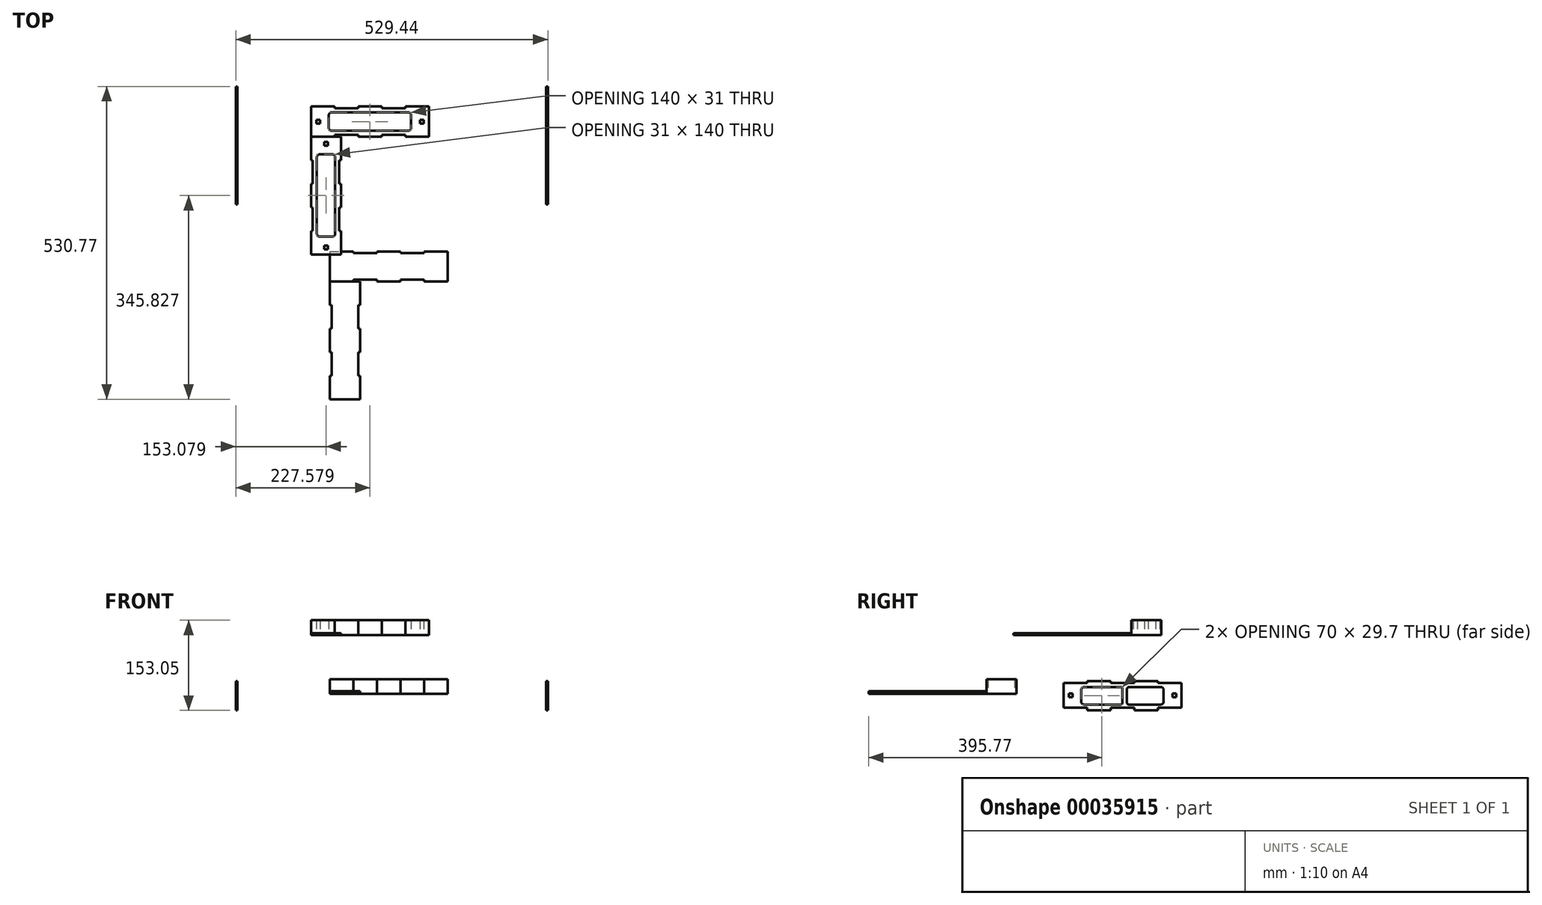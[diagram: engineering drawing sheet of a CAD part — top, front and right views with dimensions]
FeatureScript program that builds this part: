
annotation { "Feature Type Name" : "Feature", "Feature Type Description" : "" }
export const myFeature = defineFeature(function(context is Context, id is Id, definition is map)
    precondition{}
    {
        {
            var Q0;
            Q0=qCreatedBy(makeId("Top.planeOp"),FACE);
            cPlane(context, id + "F0", {"entities" : qUnion([Q0]), "cplaneType" : CPlaneType.OFFSET, "offset" : 100 * mm, "width" : 150 * mm, "height" : 150 * mm});
        }
        {
            var Q0;
            Q0=qCreatedBy(id+"F0.planeOp",FACE);
            var sketch = newSketch(context, id + "F1", { "sketchPlane" : qUnion([Q0])});
            skLineSegment(sketch, "E0", {"start": v(-137.14, 13.06) * mm, "end": v(-97.14, 13.06) * mm});
            skLineSegment(sketch, "E1", {"start": v(-97.14, 13.06) * mm, "end": v(-97.14, 10.06) * mm});
            skLineSegment(sketch, "E2", {"start": v(-97.14, 10.06) * mm, "end": v(-57.14, 10.06) * mm});
            skLineSegment(sketch, "E3", {"start": v(-57.14, 10.06) * mm, "end": v(-57.14, 13.06) * mm});
            skLineSegment(sketch, "E4", {"start": v(-57.14, 13.06) * mm, "end": v(-17.14, 13.06) * mm});
            skLineSegment(sketch, "E5", {"start": v(-17.14, 13.06) * mm, "end": v(-17.14, 10.06) * mm});
            skLineSegment(sketch, "E6", {"start": v(-17.14, 10.06) * mm, "end": v(22.86, 10.06) * mm});
            skLineSegment(sketch, "E7", {"start": v(22.86, 10.06) * mm, "end": v(22.86, 13.06) * mm});
            skLineSegment(sketch, "E8", {"start": v(22.86, 13.06) * mm, "end": v(62.86, 13.06) * mm});
            skLineSegment(sketch, "E9", {"start": v(62.86, 13.06) * mm, "end": v(62.86, -37.94) * mm});
            skLineSegment(sketch, "E10", {"start": v(62.86, -37.94) * mm, "end": v(22.86, -37.94) * mm});
            skLineSegment(sketch, "E11", {"start": v(22.86, -37.94) * mm, "end": v(22.86, -34.94) * mm});
            skLineSegment(sketch, "E12", {"start": v(22.86, -34.94) * mm, "end": v(-17.14, -34.94) * mm});
            skLineSegment(sketch, "E13", {"start": v(-17.14, -34.94) * mm, "end": v(-17.14, -37.94) * mm});
            skLineSegment(sketch, "E14", {"start": v(-17.14, -37.94) * mm, "end": v(-57.14, -37.94) * mm});
            skLineSegment(sketch, "E15", {"start": v(-57.14, -37.94) * mm, "end": v(-57.14, -34.94) * mm});
            skLineSegment(sketch, "E16", {"start": v(-57.14, -34.94) * mm, "end": v(-97.14, -34.94) * mm});
            skLineSegment(sketch, "E17", {"start": v(-97.14, -34.94) * mm, "end": v(-97.14, -37.94) * mm});
            skLineSegment(sketch, "E18", {"start": v(-97.14, -37.94) * mm, "end": v(-137.14, -37.94) * mm});
            skLineSegment(sketch, "E19", {"start": v(-137.14, 13.06) * mm, "end": v(-137.14, -37.94) * mm});
            skLineSegment(sketch, "E20.bottom", {"start": v(-102.14, -27.94) * mm, "end": v(27.86, -27.94) * mm});
            skLineSegment(sketch, "E20.top", {"start": v(-102.14, 3.06) * mm, "end": v(27.86, 3.06) * mm});
            skLineSegment(sketch, "E20.left", {"start": v(-107.14, -22.94) * mm, "end": v(-107.14, -1.94) * mm});
            skLineSegment(sketch, "E20.right", {"start": v(32.86, -22.94) * mm, "end": v(32.86, -1.94) * mm});
            skPoint(sketch, "E21.visualSharp", {"position": v(-107.14, 3.06) * mm});
            skArc(sketch, "E21.filletArc", {"start": v(-102.14, 3.06) * mm, "mid": v(-105.68, 1.6) * mm, "end": v(-107.14, -1.94) * mm});
            skPoint(sketch, "E22.visualSharp", {"position": v(-107.14, -27.94) * mm});
            skArc(sketch, "E22.filletArc", {"start": v(-107.14, -22.94) * mm, "mid": v(-105.68, -26.48) * mm, "end": v(-102.14, -27.94) * mm});
            skPoint(sketch, "E23.visualSharp", {"position": v(32.86, 3.06) * mm});
            skArc(sketch, "E23.filletArc", {"start": v(32.86, -1.94) * mm, "mid": v(31.4, 1.6) * mm, "end": v(27.86, 3.06) * mm});
            skPoint(sketch, "E24.visualSharp", {"position": v(32.86, -27.94) * mm});
            skArc(sketch, "E24.filletArc", {"start": v(27.86, -27.94) * mm, "mid": v(31.4, -26.48) * mm, "end": v(32.86, -22.94) * mm});
            skLineSegment(sketch, "E25.rect.bottom", {"start": v(47.7, -15.6) * mm, "end": v(54, -15.6) * mm});
            skLineSegment(sketch, "E25.rect.top", {"start": v(47.7, -9.3) * mm, "end": v(54, -9.3) * mm});
            skLineSegment(sketch, "E25.rect.left", {"start": v(47.7, -15.6) * mm, "end": v(47.7, -9.3) * mm});
            skLineSegment(sketch, "E25.rect.right", {"start": v(54, -15.6) * mm, "end": v(54, -9.3) * mm});
            skPoint(sketch, "E25.rect.middle", {"position": v(50.86, -12.44) * mm});
            skPoint(sketch, "E25.rect.middle.positionSnap0", {"position": v(62.86, -12.44) * mm});
            skPoint(sketch, "E25.rect.centerSnap0", {"position": v(62.86, -12.44) * mm});
            skLineSegment(sketch, "E26.rect.bottom", {"start": v(-128.3, -15.6) * mm, "end": v(-122, -15.6) * mm});
            skLineSegment(sketch, "E26.rect.top", {"start": v(-128.3, -9.3) * mm, "end": v(-122, -9.3) * mm});
            skLineSegment(sketch, "E26.rect.left", {"start": v(-128.3, -15.6) * mm, "end": v(-128.3, -9.3) * mm});
            skLineSegment(sketch, "E26.rect.right", {"start": v(-122, -15.6) * mm, "end": v(-122, -9.3) * mm});
            skPoint(sketch, "E26.rect.middle", {"position": v(-125.14, -12.44) * mm});
            skPoint(sketch, "E26.rect.middle.positionSnap0", {"position": v(-137.14, -12.44) * mm});
            skPoint(sketch, "E26.rect.centerSnap0", {"position": v(-137.14, -12.44) * mm});
            skSolve(sketch);
        }
        {
            var Q0;
            Q0 = qSketchRegion(id + "F1", true);
            extrude(context, id + "F2", {"entities" : qUnion([Q0]), "depth" : 3 * mm});
        }
        {
            var Q0;
            Q0=qCreatedBy(makeId("Front.planeOp"),FACE);
            cPlane(context, id + "F3", {"entities" : qUnion([Q0]), "cplaneType" : CPlaneType.OFFSET, "offset" : 150 * mm, "width" : 150 * mm, "height" : 150 * mm});
        }
        {
            var Q0;
            Q0=qCreatedBy(id+"F3.planeOp",FACE);
            var sketch = newSketch(context, id + "F4", { "sketchPlane" : qUnion([Q0])});
            skLineSegment(sketch, "E27", {"start": v(-261.72, -23.35) * mm, "end": v(-261.72, 18.65) * mm});
            skLineSegment(sketch, "E28", {"start": v(-261.72, 18.65) * mm, "end": v(-221.72, 18.65) * mm});
            skLineSegment(sketch, "E29", {"start": v(-221.72, 18.65) * mm, "end": v(-221.72, 21.65) * mm});
            skLineSegment(sketch, "E30", {"start": v(-221.72, 21.65) * mm, "end": v(-181.72, 21.65) * mm});
            skLineSegment(sketch, "E31", {"start": v(-181.72, 21.65) * mm, "end": v(-181.72, 18.65) * mm});
            skLineSegment(sketch, "E32", {"start": v(-181.72, 18.65) * mm, "end": v(-141.72, 18.65) * mm});
            skLineSegment(sketch, "E33", {"start": v(-141.72, 18.65) * mm, "end": v(-141.72, 21.65) * mm});
            skLineSegment(sketch, "E34", {"start": v(-141.72, 21.65) * mm, "end": v(-101.72, 21.65) * mm});
            skLineSegment(sketch, "E35", {"start": v(-101.72, 21.65) * mm, "end": v(-101.72, 18.65) * mm});
            skLineSegment(sketch, "E36", {"start": v(-101.72, 18.65) * mm, "end": v(-61.72, 18.65) * mm});
            skLineSegment(sketch, "E37", {"start": v(-61.72, 18.65) * mm, "end": v(-61.72, -23.35) * mm});
            skLineSegment(sketch, "E38", {"start": v(-61.72, -23.35) * mm, "end": v(-101.72, -23.35) * mm});
            skLineSegment(sketch, "E39", {"start": v(-101.72, -23.35) * mm, "end": v(-101.72, -28.05) * mm});
            skLineSegment(sketch, "E40", {"start": v(-101.72, -28.05) * mm, "end": v(-141.72, -28.05) * mm});
            skLineSegment(sketch, "E41", {"start": v(-141.72, -28.05) * mm, "end": v(-141.72, -23.35) * mm});
            skLineSegment(sketch, "E42", {"start": v(-141.72, -23.35) * mm, "end": v(-181.72, -23.35) * mm});
            skLineSegment(sketch, "E43", {"start": v(-181.72, -23.35) * mm, "end": v(-181.72, -28.05) * mm});
            skLineSegment(sketch, "E44", {"start": v(-181.72, -28.05) * mm, "end": v(-221.72, -28.05) * mm});
            skLineSegment(sketch, "E45", {"start": v(-221.72, -28.05) * mm, "end": v(-221.72, -23.35) * mm});
            skLineSegment(sketch, "E46", {"start": v(-221.72, -23.35) * mm, "end": v(-261.72, -23.35) * mm});
            skLineSegment(sketch, "E47.bottom", {"start": v(-226.72, 11.65) * mm, "end": v(-164.72, 11.65) * mm});
            skLineSegment(sketch, "E47.top", {"start": v(-226.72, -18.05) * mm, "end": v(-164.72, -18.05) * mm});
            skLineSegment(sketch, "E47.left", {"start": v(-231.72, 6.65) * mm, "end": v(-231.72, -13.05) * mm});
            skLineSegment(sketch, "E47.right", {"start": v(-161.72, 8.65) * mm, "end": v(-161.72, -15.05) * mm});
            skLineSegment(sketch, "E48.bottom", {"start": v(-150.95, 11.65) * mm, "end": v(-96.72, 11.65) * mm});
            skLineSegment(sketch, "E48.top", {"start": v(-150.95, -18.05) * mm, "end": v(-96.72, -18.05) * mm});
            skLineSegment(sketch, "E48.left", {"start": v(-153.95, 8.65) * mm, "end": v(-153.95, -15.05) * mm});
            skLineSegment(sketch, "E48.right", {"start": v(-91.72, 6.65) * mm, "end": v(-91.72, -13.05) * mm});
            skPoint(sketch, "E49.visualSharp", {"position": v(-231.72, 11.65) * mm});
            skArc(sketch, "E49.filletArc", {"start": v(-226.72, 11.65) * mm, "mid": v(-230.26, 10.18) * mm, "end": v(-231.72, 6.65) * mm});
            skPoint(sketch, "E50.visualSharp", {"position": v(-231.72, -18.05) * mm});
            skArc(sketch, "E50.filletArc", {"start": v(-231.72, -13.05) * mm, "mid": v(-230.26, -16.59) * mm, "end": v(-226.72, -18.05) * mm});
            skPoint(sketch, "E51.visualSharp", {"position": v(-91.72, 11.65) * mm});
            skArc(sketch, "E51.filletArc", {"start": v(-91.72, 6.65) * mm, "mid": v(-93.18, 10.18) * mm, "end": v(-96.72, 11.65) * mm});
            skPoint(sketch, "E52.visualSharp", {"position": v(-91.72, -18.05) * mm});
            skArc(sketch, "E52.filletArc", {"start": v(-96.72, -18.05) * mm, "mid": v(-93.18, -16.59) * mm, "end": v(-91.72, -13.05) * mm});
            skPoint(sketch, "E53.visualSharp", {"position": v(-153.95, 11.65) * mm});
            skArc(sketch, "E53.filletArc", {"start": v(-150.95, 11.65) * mm, "mid": v(-153.07, 10.77) * mm, "end": v(-153.95, 8.65) * mm});
            skPoint(sketch, "E54.visualSharp", {"position": v(-153.95, -18.05) * mm});
            skArc(sketch, "E54.filletArc", {"start": v(-153.95, -15.05) * mm, "mid": v(-153.07, -17.18) * mm, "end": v(-150.95, -18.05) * mm});
            skPoint(sketch, "E55.visualSharp", {"position": v(-161.72, -18.05) * mm});
            skArc(sketch, "E55.filletArc", {"start": v(-164.72, -18.05) * mm, "mid": v(-162.6, -17.18) * mm, "end": v(-161.72, -15.05) * mm});
            skPoint(sketch, "E56.visualSharp", {"position": v(-161.72, 11.65) * mm});
            skArc(sketch, "E56.filletArc", {"start": v(-161.72, 8.65) * mm, "mid": v(-162.6, 10.77) * mm, "end": v(-164.72, 11.65) * mm});
            skLineSegment(sketch, "E57.rect.bottom", {"start": v(-246.57, 0.8) * mm, "end": v(-252.87, 0.8) * mm});
            skLineSegment(sketch, "E57.rect.top", {"start": v(-246.57, -5.5) * mm, "end": v(-252.87, -5.5) * mm});
            skLineSegment(sketch, "E57.rect.left", {"start": v(-246.57, 0.8) * mm, "end": v(-246.57, -5.5) * mm});
            skLineSegment(sketch, "E57.rect.right", {"start": v(-252.87, 0.8) * mm, "end": v(-252.87, -5.5) * mm});
            skPoint(sketch, "E57.rect.middle", {"position": v(-249.72, -2.35) * mm});
            skPoint(sketch, "E57.rect.middle.positionSnap0", {"position": v(-261.72, -2.35) * mm});
            skPoint(sketch, "E57.rect.centerSnap0", {"position": v(-261.72, -2.35) * mm});
            skLineSegment(sketch, "E58.rect.bottom", {"start": v(-70.57, 0.8) * mm, "end": v(-76.87, 0.8) * mm});
            skLineSegment(sketch, "E58.rect.top", {"start": v(-70.57, -5.5) * mm, "end": v(-76.87, -5.5) * mm});
            skLineSegment(sketch, "E58.rect.left", {"start": v(-70.57, 0.8) * mm, "end": v(-70.57, -5.5) * mm});
            skLineSegment(sketch, "E58.rect.right", {"start": v(-76.87, 0.8) * mm, "end": v(-76.87, -5.5) * mm});
            skPoint(sketch, "E58.rect.middle", {"position": v(-73.72, -2.35) * mm});
            skPoint(sketch, "E58.rect.middle.positionSnap0", {"position": v(-61.72, -2.35) * mm});
            skPoint(sketch, "E58.rect.centerSnap0", {"position": v(-61.72, -2.35) * mm});
            skSolve(sketch);
        }
        {
            var Q0;
            Q0 = qSketchRegion(id + "F4", true);
            extrude(context, id + "F5", {"entities" : qUnion([Q0]), "depth" : 3 * mm});
        }
        {
            var Q0;
            Q0=qCreatedBy(makeId("Top.planeOp"),FACE);
            var sketch = newSketch(context, id + "F6", { "sketchPlane" : qUnion([Q0])});
            skLineSegment(sketch, "E59", {"start": v(94.97, -232.77) * mm, "end": v(94.97, -283.77) * mm});
            skLineSegment(sketch, "E60", {"start": v(54.97, -232.77) * mm, "end": v(94.97, -232.77) * mm});
            skLineSegment(sketch, "E61", {"start": v(14.97, -283.77) * mm, "end": v(-25.03, -283.77) * mm});
            skLineSegment(sketch, "E62", {"start": v(14.97, -235.77) * mm, "end": v(54.97, -235.77) * mm});
            skLineSegment(sketch, "E63", {"start": v(-105.03, -232.77) * mm, "end": v(-105.03, -283.77) * mm});
            skLineSegment(sketch, "E64", {"start": v(-65.03, -283.77) * mm, "end": v(-105.03, -283.77) * mm});
            skLineSegment(sketch, "E65", {"start": v(-25.03, -280.77) * mm, "end": v(-65.03, -280.77) * mm});
            skLineSegment(sketch, "E66", {"start": v(54.97, -280.77) * mm, "end": v(14.97, -280.77) * mm});
            skLineSegment(sketch, "E67", {"start": v(94.97, -283.77) * mm, "end": v(54.97, -283.77) * mm});
            skLineSegment(sketch, "E68", {"start": v(-105.03, -232.77) * mm, "end": v(-65.03, -232.77) * mm});
            skLineSegment(sketch, "E69", {"start": v(-65.03, -235.77) * mm, "end": v(-25.03, -235.77) * mm});
            skLineSegment(sketch, "E70", {"start": v(-25.03, -232.77) * mm, "end": v(14.97, -232.77) * mm});
            skLineSegment(sketch, "E71", {"start": v(14.97, -232.77) * mm, "end": v(14.97, -235.77) * mm});
            skLineSegment(sketch, "E72", {"start": v(-65.03, -280.77) * mm, "end": v(-65.03, -283.77) * mm});
            skLineSegment(sketch, "E73", {"start": v(54.97, -235.77) * mm, "end": v(54.97, -232.77) * mm});
            skLineSegment(sketch, "E74", {"start": v(14.97, -280.77) * mm, "end": v(14.97, -283.77) * mm});
            skLineSegment(sketch, "E75", {"start": v(54.97, -283.77) * mm, "end": v(54.97, -280.77) * mm});
            skLineSegment(sketch, "E76", {"start": v(-25.03, -283.77) * mm, "end": v(-25.03, -280.77) * mm});
            skLineSegment(sketch, "E77", {"start": v(-65.03, -232.77) * mm, "end": v(-65.03, -235.77) * mm});
            skLineSegment(sketch, "E78", {"start": v(-25.03, -235.77) * mm, "end": v(-25.03, -232.77) * mm});
            skSolve(sketch);
        }
        {
            var Q0;
            Q0=makeQuery(id+"F6.imprint","IMPRINT",FACE,{"disambiguationData":[TD([[makeQuery(id+"F6.imprint","IMPRINT",EDGE,{"derivedFrom":sQuery(id+"F6.wireOp",EDGE,"E59")}),-1.0]])]});
            extrude(context, id + "F7", {"entities" : qUnion([Q0]), "depth" : 4.7 * mm});
        }
        {
            var Q0;
            Q0=makeQuery(id+"F2.opExtrude","SWEPT_BODY",BODY,{"disambiguationData":[OSD([sQuery(id+"F1.wireOp",EDGE,"E0"),sQuery(id+"F1.wireOp",EDGE,"E1"),sQuery(id+"F1.wireOp",EDGE,"E2"),sQuery(id+"F1.wireOp",EDGE,"E3"),sQuery(id+"F1.wireOp",EDGE,"E4"),sQuery(id+"F1.wireOp",EDGE,"E5"),sQuery(id+"F1.wireOp",EDGE,"E6"),sQuery(id+"F1.wireOp",EDGE,"E7"),sQuery(id+"F1.wireOp",EDGE,"E8"),sQuery(id+"F1.wireOp",EDGE,"E9"),sQuery(id+"F1.wireOp",EDGE,"E10"),sQuery(id+"F1.wireOp",EDGE,"E11"),sQuery(id+"F1.wireOp",EDGE,"E12"),sQuery(id+"F1.wireOp",EDGE,"E13"),sQuery(id+"F1.wireOp",EDGE,"E14"),sQuery(id+"F1.wireOp",EDGE,"E15"),sQuery(id+"F1.wireOp",EDGE,"E16"),sQuery(id+"F1.wireOp",EDGE,"E17"),sQuery(id+"F1.wireOp",EDGE,"E18"),sQuery(id+"F1.wireOp",EDGE,"E19"),sQuery(id+"F1.wireOp",EDGE,"E20.bottom"),sQuery(id+"F1.wireOp",EDGE,"E20.top"),sQuery(id+"F1.wireOp",EDGE,"E20.left"),sQuery(id+"F1.wireOp",EDGE,"E20.right"),sQuery(id+"F1.wireOp",EDGE,"E21.filletArc"),sQuery(id+"F1.wireOp",EDGE,"E22.filletArc"),sQuery(id+"F1.wireOp",EDGE,"E23.filletArc"),sQuery(id+"F1.wireOp",EDGE,"E24.filletArc")])]});
            var Q1;
            Q1=makeQuery(id+"F2.opExtrude","SWEPT_EDGE",EDGE,{"disambiguationData":[OSD([sQuery(id+"F1.wireOp",EDGE,"E18"),sQuery(id+"F1.wireOp",EDGE,"E19")])]});
            transform(context, id + "F8", {"entities" : qUnion([Q0]), "transformType" : TransformType.ROTATION, "transformAxis" : qUnion([Q1]), "angle" : 90 * degree, "makeCopy" : false});
        }
        {
            var Q0;
            Q0=makeQuery(id+"F7.opExtrude","SWEPT_BODY",BODY,{"disambiguationData":[OSD([sQuery(id+"F6.wireOp",EDGE,"E59"),sQuery(id+"F6.wireOp",EDGE,"E60"),sQuery(id+"F6.wireOp",EDGE,"E61"),sQuery(id+"F6.wireOp",EDGE,"E62"),sQuery(id+"F6.wireOp",EDGE,"E63"),sQuery(id+"F6.wireOp",EDGE,"E64"),sQuery(id+"F6.wireOp",EDGE,"E65"),sQuery(id+"F6.wireOp",EDGE,"E66"),sQuery(id+"F6.wireOp",EDGE,"E67"),sQuery(id+"F6.wireOp",EDGE,"E68"),sQuery(id+"F6.wireOp",EDGE,"E69"),sQuery(id+"F6.wireOp",EDGE,"E70"),sQuery(id+"F6.wireOp",EDGE,"E71"),sQuery(id+"F6.wireOp",EDGE,"E72"),sQuery(id+"F6.wireOp",EDGE,"E73"),sQuery(id+"F6.wireOp",EDGE,"E74"),sQuery(id+"F6.wireOp",EDGE,"E75"),sQuery(id+"F6.wireOp",EDGE,"E76"),sQuery(id+"F6.wireOp",EDGE,"E77"),sQuery(id+"F6.wireOp",EDGE,"E78")])]});
            var Q1;
            Q1=makeQuery(id+"F7.opExtrude","SWEPT_EDGE",EDGE,{"disambiguationData":[OSD([sQuery(id+"F6.wireOp",EDGE,"E63"),sQuery(id+"F6.wireOp",EDGE,"E64")])]});
            transform(context, id + "F9", {"entities" : qUnion([Q0]), "transformType" : TransformType.ROTATION, "transformAxis" : qUnion([Q1]), "angle" : 90 * degree, "makeCopy" : false});
        }
        {
            var Q0;
            Q0=makeQuery(id+"F5.opExtrude","SWEPT_BODY",BODY,{"disambiguationData":[OSD([sQuery(id+"F4.wireOp",EDGE,"E27"),sQuery(id+"F4.wireOp",EDGE,"E28"),sQuery(id+"F4.wireOp",EDGE,"E29"),sQuery(id+"F4.wireOp",EDGE,"E30"),sQuery(id+"F4.wireOp",EDGE,"E31"),sQuery(id+"F4.wireOp",EDGE,"E32"),sQuery(id+"F4.wireOp",EDGE,"E33"),sQuery(id+"F4.wireOp",EDGE,"E34"),sQuery(id+"F4.wireOp",EDGE,"E35"),sQuery(id+"F4.wireOp",EDGE,"E36"),sQuery(id+"F4.wireOp",EDGE,"E37"),sQuery(id+"F4.wireOp",EDGE,"E38"),sQuery(id+"F4.wireOp",EDGE,"E39"),sQuery(id+"F4.wireOp",EDGE,"E40"),sQuery(id+"F4.wireOp",EDGE,"E41"),sQuery(id+"F4.wireOp",EDGE,"E42"),sQuery(id+"F4.wireOp",EDGE,"E43"),sQuery(id+"F4.wireOp",EDGE,"E44"),sQuery(id+"F4.wireOp",EDGE,"E45"),sQuery(id+"F4.wireOp",EDGE,"E46"),sQuery(id+"F4.wireOp",EDGE,"7fbabfab-6c45-4351-a13d-65926b73b169.bottom"),sQuery(id+"F4.wireOp",EDGE,"7fbabfab-6c45-4351-a13d-65926b73b169.top"),sQuery(id+"F4.wireOp",EDGE,"7fbabfab-6c45-4351-a13d-65926b73b169.left"),sQuery(id+"F4.wireOp",EDGE,"7fbabfab-6c45-4351-a13d-65926b73b169.right"),sQuery(id+"F4.wireOp",EDGE,"bc9e853f-3614-4c7b-95ac-c1f526d06f9d.bottom"),sQuery(id+"F4.wireOp",EDGE,"bc9e853f-3614-4c7b-95ac-c1f526d06f9d.top"),sQuery(id+"F4.wireOp",EDGE,"bc9e853f-3614-4c7b-95ac-c1f526d06f9d.left"),sQuery(id+"F4.wireOp",EDGE,"bc9e853f-3614-4c7b-95ac-c1f526d06f9d.right"),sQuery(id+"F4.wireOp",EDGE,"9d363461-d9c7-42ad-a605-f10a583b7adf.filletArc"),sQuery(id+"F4.wireOp",EDGE,"a8185aef-b156-4268-98df-fd60d99d2e8b.filletArc"),sQuery(id+"F4.wireOp",EDGE,"17aa48d8-23c2-4526-90ac-4948f552f9d6.filletArc"),sQuery(id+"F4.wireOp",EDGE,"ec2dc547-445c-4b10-b0b5-5fbef85a2b8e.filletArc"),sQuery(id+"F4.wireOp",EDGE,"308059fb-494a-4663-8d27-ab8e5de39cd5.filletArc"),sQuery(id+"F4.wireOp",EDGE,"7f48fe49-b43d-4b02-bc32-553ec1c7f7b5.filletArc"),sQuery(id+"F4.wireOp",EDGE,"39a5a2ae-93e5-4ad9-8a0c-e8c8752d564a.filletArc"),sQuery(id+"F4.wireOp",EDGE,"36d556c5-8a39-45bb-97b7-d6d2a9260684.filletArc")])]});
            var Q1;
            Q1=makeQuery(id+"F5.opExtrude","CAP_EDGE",EDGE,{"disambiguationData":[OSD([sQuery(id+"F4.wireOp",EDGE,"E27")])],"isStart":false});
            transform(context, id + "F10", {"entities" : qUnion([Q0]), "transformType" : TransformType.ROTATION, "transformAxis" : qUnion([Q1]), "angle" : 90 * degree, "makeCopy" : false});
        }
        {
            var Q0;
            Q0=makeQuery(id+"F5.opExtrude","SWEPT_BODY",BODY,{"disambiguationData":[OSD([sQuery(id+"F4.wireOp",EDGE,"E27"),sQuery(id+"F4.wireOp",EDGE,"E28"),sQuery(id+"F4.wireOp",EDGE,"E29"),sQuery(id+"F4.wireOp",EDGE,"E30"),sQuery(id+"F4.wireOp",EDGE,"E31"),sQuery(id+"F4.wireOp",EDGE,"E32"),sQuery(id+"F4.wireOp",EDGE,"E33"),sQuery(id+"F4.wireOp",EDGE,"E34"),sQuery(id+"F4.wireOp",EDGE,"E35"),sQuery(id+"F4.wireOp",EDGE,"E36"),sQuery(id+"F4.wireOp",EDGE,"E37"),sQuery(id+"F4.wireOp",EDGE,"E38"),sQuery(id+"F4.wireOp",EDGE,"E39"),sQuery(id+"F4.wireOp",EDGE,"E40"),sQuery(id+"F4.wireOp",EDGE,"E41"),sQuery(id+"F4.wireOp",EDGE,"E42"),sQuery(id+"F4.wireOp",EDGE,"E43"),sQuery(id+"F4.wireOp",EDGE,"E44"),sQuery(id+"F4.wireOp",EDGE,"E45"),sQuery(id+"F4.wireOp",EDGE,"E46"),sQuery(id+"F4.wireOp",EDGE,"7fbabfab-6c45-4351-a13d-65926b73b169.bottom"),sQuery(id+"F4.wireOp",EDGE,"7fbabfab-6c45-4351-a13d-65926b73b169.top"),sQuery(id+"F4.wireOp",EDGE,"7fbabfab-6c45-4351-a13d-65926b73b169.left"),sQuery(id+"F4.wireOp",EDGE,"7fbabfab-6c45-4351-a13d-65926b73b169.right"),sQuery(id+"F4.wireOp",EDGE,"bc9e853f-3614-4c7b-95ac-c1f526d06f9d.bottom"),sQuery(id+"F4.wireOp",EDGE,"bc9e853f-3614-4c7b-95ac-c1f526d06f9d.top"),sQuery(id+"F4.wireOp",EDGE,"bc9e853f-3614-4c7b-95ac-c1f526d06f9d.left"),sQuery(id+"F4.wireOp",EDGE,"bc9e853f-3614-4c7b-95ac-c1f526d06f9d.right"),sQuery(id+"F4.wireOp",EDGE,"9d363461-d9c7-42ad-a605-f10a583b7adf.filletArc"),sQuery(id+"F4.wireOp",EDGE,"a8185aef-b156-4268-98df-fd60d99d2e8b.filletArc"),sQuery(id+"F4.wireOp",EDGE,"17aa48d8-23c2-4526-90ac-4948f552f9d6.filletArc"),sQuery(id+"F4.wireOp",EDGE,"ec2dc547-445c-4b10-b0b5-5fbef85a2b8e.filletArc"),sQuery(id+"F4.wireOp",EDGE,"308059fb-494a-4663-8d27-ab8e5de39cd5.filletArc"),sQuery(id+"F4.wireOp",EDGE,"7f48fe49-b43d-4b02-bc32-553ec1c7f7b5.filletArc"),sQuery(id+"F4.wireOp",EDGE,"39a5a2ae-93e5-4ad9-8a0c-e8c8752d564a.filletArc"),sQuery(id+"F4.wireOp",EDGE,"36d556c5-8a39-45bb-97b7-d6d2a9260684.filletArc")])]});
            var Q1;
            Q1=qCreatedBy(makeId("Right.planeOp"),FACE);
            mirror(context, id + "F11", {"entities" : qUnion([Q0]), "mirrorPlane" : qUnion([Q1])});
        }
        {
            var Q0;
            Q0 = qSketchRegion(id + "F1", true);
            extrude(context, id + "F12", {"entities" : qUnion([Q0]), "depth" : 25 * mm});
        }
        {
            var Q0;
            Q0 = qSketchRegion(id + "F6", true);
            extrude(context, id + "F13", {"entities" : qUnion([Q0]), "depth" : 25 * mm});
        }
    });
